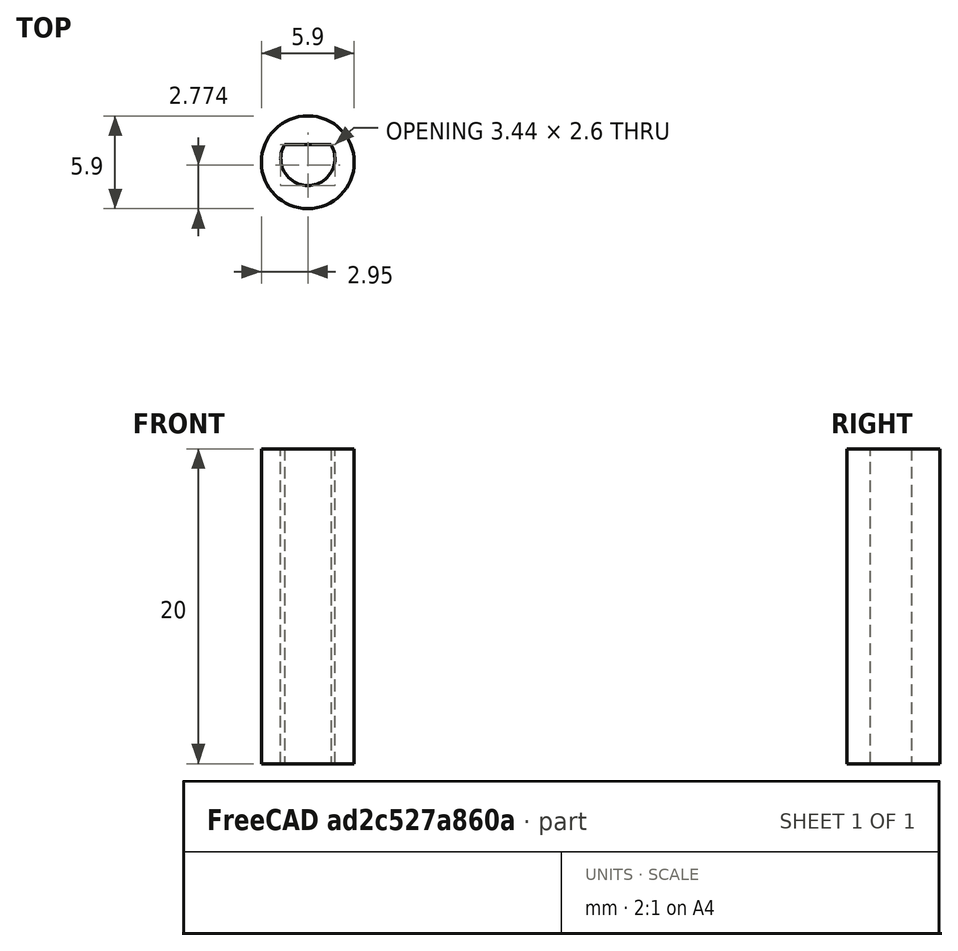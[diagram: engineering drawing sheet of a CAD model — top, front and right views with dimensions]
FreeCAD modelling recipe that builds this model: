
FCSTD DOCUMENT  (FreeCAD 0.18R4 (GitTag))
Label: Shaft Attachment
License: All rights reserved
LicenseURL: http://en.wikipedia.org/wiki/All_rights_reserved
objects: Sketcher::SketchObject×2, PartDesign::Pad×1, PartDesign::Pocket×1, PartDesign::Body×1
note: 7 computed .brp shape members not serialized (recipe doc carries the construction recipe); baked Part::Feature solids carry a one-line shape summary decoded from their .brp

FEATURE [Sketcher::SketchObject] Sketch
  MapMode = 5
  Support = -> [XY_Plane]
  sketch-geometry (1):
    g0: Circle CenterX=0 CenterY=0 CenterZ=0 NormalX=0 NormalY=0 NormalZ=1 AngleXU=0 Radius=2.95
  constraints (1):
    c: Radius(g0) = 2.95
FEATURE [PartDesign::Pad] Pad
  Length = 20
  Length2 = 100
  Profile = -> Sketch
  Type = 0
FEATURE [Sketcher::SketchObject] Sketch001
  MapMode = 5
  Placement = pos=(0,0,20) rot=(0,0,1;0rad)
  Support = -> [Pad]
  sketch-geometry (3):
    g0: GeomPoint X=0 Y=1.12 Z=0
    g1: ArcOfCircle CenterX=-0.000196761 CenterY=0.245238 CenterZ=0 NormalX=0 NormalY=0 NormalZ=1 AngleXU=0 Radius=1.72 StartAngle=2.608 EndAngle=6.81838
    g2: LineSegment StartX=-1.48109 StartY=1.12008 StartZ=0 EndX=1.47929 EndY=1.12246 EndZ=0
  constraints (3):
    c: Radius(g1) = 1.72
    c: Coincident(g1,g2)
    c: Coincident(g1,g2)
FEATURE [PartDesign::Pocket] Pocket
  BaseFeature = -> Pad
  Length = 20
  Length2 = 100
  Profile = -> Sketch001
  Type = 0
FEATURE [PartDesign::Body] Body
  Group = -> [Sketch,Pad,Sketch001,Pocket]
  Origin = -> Origin
  Tip = -> Pocket
